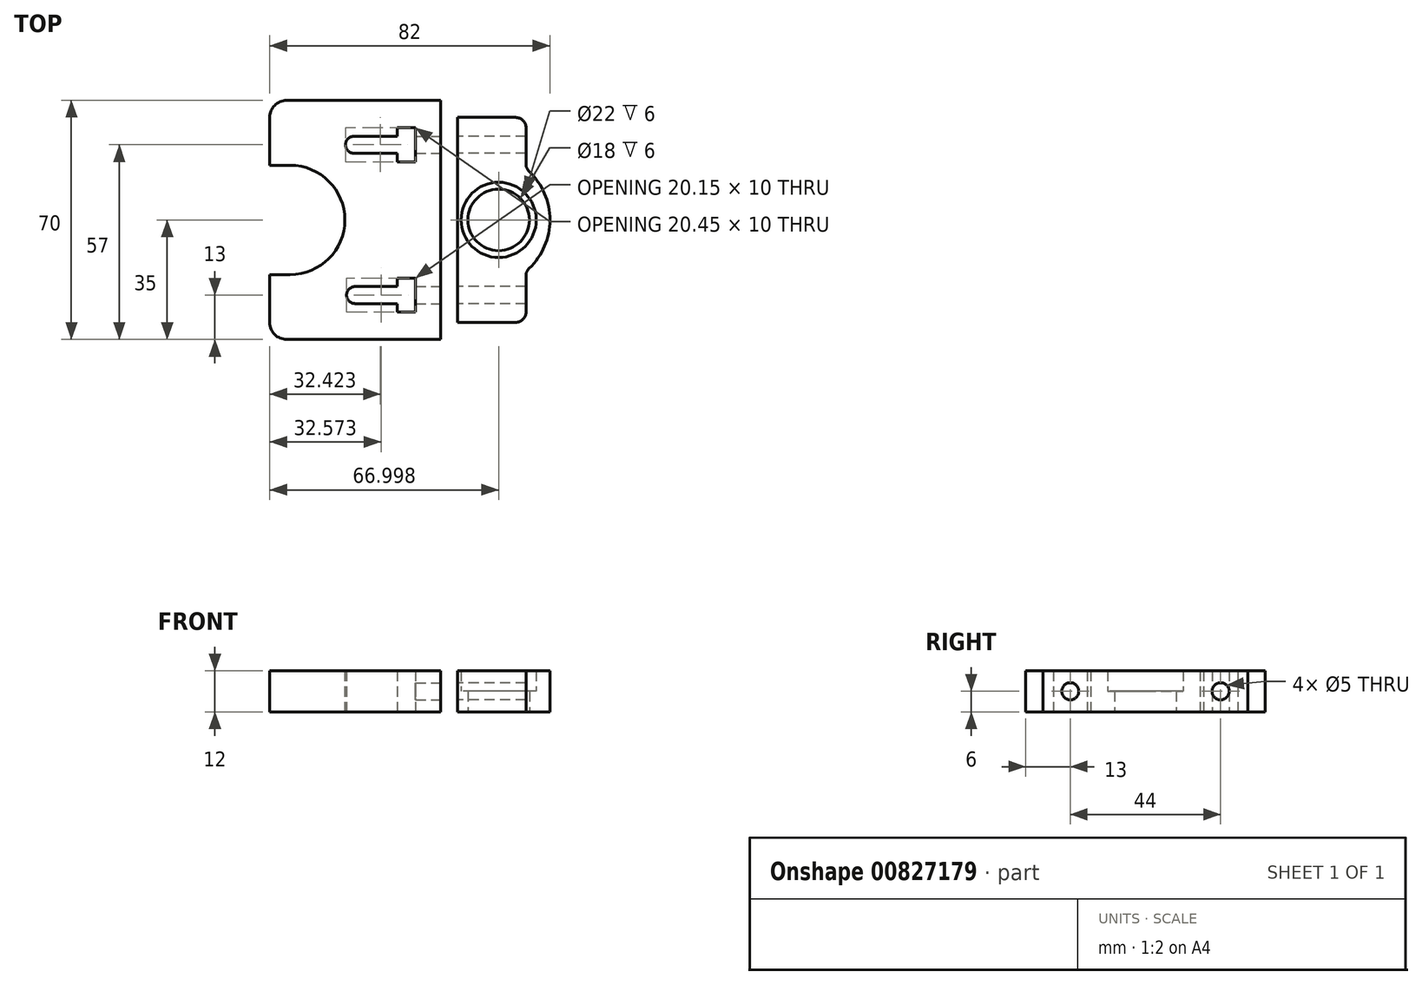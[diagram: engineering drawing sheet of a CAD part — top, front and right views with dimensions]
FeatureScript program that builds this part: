
annotation { "Feature Type Name" : "Feature", "Feature Type Description" : "" }
export const myFeature = defineFeature(function(context is Context, id is Id, definition is map)
    precondition{}
    {
        {
            var Q0;
            Q0=qCreatedBy(makeId("Top.planeOp"),FACE);
            var sketch = newSketch(context, id + "F0", { "sketchPlane" : qUnion([Q0])});
            skLineSegment(sketch, "E0.bottom", {"start": v(5.25, 143.35) * mm, "end": v(11.25, 143.35) * mm, "construction": true});
            skLineSegment(sketch, "E0.top", {"start": v(5.25, -56.65) * mm, "end": v(11.25, -56.65) * mm, "construction": true});
            skLineSegment(sketch, "E1", {"start": v(11.25, 0) * mm, "end": v(23.25, 0) * mm, "construction": true});
            skCircle(sketch, "E2", {"center": v(23.25, 0) * mm, "radius": 11 * mm, "construction": true});
            skLineSegment(sketch, "E3", {"start": v(23.25, 0) * mm, "end": v(-37.75, 0) * mm, "construction": true});
            skCircle(sketch, "E4", {"center": v(-37.75, 0) * mm, "radius": 12.5 * mm, "construction": true});
            skCircle(sketch, "E5", {"center": v(23.25, 0) * mm, "radius": 12.5 * mm, "construction": true});
            skCircle(sketch, "E6", {"center": v(-37.75, 0) * mm, "radius": 28 * mm, "construction": true});
            skLineSegment(sketch, "E7", {"start": v(6.25, 0) * mm, "end": v(6.25, 35) * mm});
            skLineSegment(sketch, "E8", {"start": v(6.25, 35) * mm, "end": v(-43.75, 35) * mm});
            skLineSegment(sketch, "E9", {"start": v(-43.75, 35) * mm, "end": v(-43.75, 16) * mm});
            skLineSegment(sketch, "E10", {"start": v(-43.75, -35) * mm, "end": v(6.25, -35) * mm});
            skLineSegment(sketch, "E11", {"start": v(6.25, -35) * mm, "end": v(6.25, 0) * mm});
            skLineSegment(sketch, "E12", {"start": v(-37.75, 16) * mm, "end": v(-43.75, 16) * mm});
            skLineSegment(sketch, "E13", {"start": v(-37.75, -16) * mm, "end": v(-43.75, -16) * mm});
            skArc(sketch, "E14.trimOffspring", {"start": v(-37.75, -16) * mm, "mid": v(-21.75, 0) * mm, "end": v(-37.75, 16) * mm});
            skLineSegment(sketch, "E15.trimOffspring", {"start": v(-43.75, -16) * mm, "end": v(-43.75, -35) * mm});
            skLineSegment(sketch, "E16", {"start": v(-37.75, -28) * mm, "end": v(6.25, -28) * mm, "construction": true});
            skLineSegment(sketch, "E17", {"start": v(-37.75, 28) * mm, "end": v(6.25, 28) * mm, "construction": true});
            skLineSegment(sketch, "E18", {"start": v(-37.75, 0) * mm, "end": v(-37.75, 16) * mm, "construction": true});
            skLineSegment(sketch, "E19", {"start": v(-37.75, 0) * mm, "end": v(-37.75, -16) * mm, "construction": true});
            skLineSegment(sketch, "E20", {"start": v(-37.75, 0) * mm, "end": v(-7.75, 0) * mm, "construction": true});
            skLineSegment(sketch, "E21", {"start": v(-7.75, 0) * mm, "end": v(-7.75, 22) * mm, "construction": true});
            skLineSegment(sketch, "E22", {"start": v(-7.75, 0) * mm, "end": v(-7.75, -22) * mm, "construction": true});
            skLineSegment(sketch, "E23", {"start": v(-7.75, 22) * mm, "end": v(-13.25, 22) * mm, "construction": true});
            skLineSegment(sketch, "E24", {"start": v(-7.75, -22) * mm, "end": v(-13.25, -22) * mm, "construction": true});
            skCircle(sketch, "E25", {"center": v(-13.25, -22) * mm, "radius": 2.5 * mm, "construction": true});
            skCircle(sketch, "E26", {"center": v(-13.25, 22) * mm, "radius": 2.5 * mm, "construction": true});
            skLineSegment(sketch, "E27", {"start": v(-13.25, -22) * mm, "end": v(-18.75, -22) * mm, "construction": true});
            skArc(sketch, "E28", {"start": v(-18.75, -19.5) * mm, "mid": v(-21.25, -22) * mm, "end": v(-18.75, -24.5) * mm});
            skLineSegment(sketch, "E29", {"start": v(-18.75, -22) * mm, "end": v(-18.75, -19.5) * mm, "construction": true});
            skLineSegment(sketch, "E30", {"start": v(-18.75, -19.5) * mm, "end": v(-18.75, -24.5) * mm, "construction": true});
            skLineSegment(sketch, "E31", {"start": v(-7.75, -22) * mm, "end": v(-7.75, -24.5) * mm, "construction": true});
            skLineSegment(sketch, "E32", {"start": v(-18.75, -19.5) * mm, "end": v(-6.4, -19.5) * mm});
            skLineSegment(sketch, "E33", {"start": v(-18.75, -24.5) * mm, "end": v(-6.4, -24.5) * mm});
            skArc(sketch, "E34", {"start": v(-19.05, 24.5) * mm, "mid": v(-21.55, 22) * mm, "end": v(-19.05, 19.5) * mm});
            skLineSegment(sketch, "E35", {"start": v(-13.25, 22) * mm, "end": v(31.35, 22) * mm, "construction": true});
            skLineSegment(sketch, "E36", {"start": v(-13.25, -22) * mm, "end": v(47, -22) * mm, "construction": true});
            skLineSegment(sketch, "E37", {"start": v(6.25, 22) * mm, "end": v(-3.75, 22) * mm, "construction": true});
            skLineSegment(sketch, "E38", {"start": v(6.25, -22) * mm, "end": v(-3.75, -22) * mm, "construction": true});
            skLineSegment(sketch, "E39.bottom", {"start": v(-1.1, 27) * mm, "end": v(-6.4, 27) * mm});
            skLineSegment(sketch, "E39.top", {"start": v(-1.1, 17) * mm, "end": v(-6.4, 17) * mm});
            skLineSegment(sketch, "E39.left", {"start": v(-1.1, 27) * mm, "end": v(-1.1, 17) * mm});
            skLineSegment(sketch, "E39.right", {"start": v(-6.4, 27) * mm, "end": v(-6.4, 17) * mm});
            skPoint(sketch, "E39.middle", {"position": v(-3.75, 22) * mm});
            skLineSegment(sketch, "E40.bottom", {"start": v(-1.1, -17) * mm, "end": v(-6.4, -17) * mm});
            skLineSegment(sketch, "E40.top", {"start": v(-1.1, -27) * mm, "end": v(-6.4, -27) * mm});
            skLineSegment(sketch, "E40.left", {"start": v(-1.1, -17) * mm, "end": v(-1.1, -27) * mm});
            skLineSegment(sketch, "E40.right", {"start": v(-6.4, -17) * mm, "end": v(-6.4, -27) * mm});
            skPoint(sketch, "E40.middle", {"position": v(-3.75, -22) * mm});
            skLineSegment(sketch, "E41", {"start": v(-19.05, 24.5) * mm, "end": v(-6.4, 24.5) * mm});
            skLineSegment(sketch, "E42", {"start": v(-19.05, 19.5) * mm, "end": v(-6.4, 19.5) * mm});
            skSolve(sketch);
        }
        {
            var Q0;
            Q0=makeQuery(id+"F0.imprint","IMPRINT",FACE,{"disambiguationData":[TD([[makeQuery(id+"F0.imprint","IMPRINT",EDGE,{"derivedFrom":sQuery(id+"F0.wireOp",EDGE,"E7")}),1.0]])]});
            extrude(context, id + "F1", {"entities" : qUnion([Q0]), "depth" : 12 * mm, "offsetDistance" : 25 * mm});
        }
        {
            var Q0;
            Q0=makeQuery(id+"F1.opExtrude","SWEPT_FACE",FACE,{"disambiguationData":[OSD([sQuery(id+"F0.wireOp",EDGE,"E7"),sQuery(id+"F0.wireOp",EDGE,"E11")])]});
            var sketch = newSketch(context, id + "F2", { "sketchPlane" : qUnion([Q0])});
            skLineSegment(sketch, "E43", {"start": v(-35, 12) * mm, "end": v(-22, 12) * mm, "construction": true});
            skLineSegment(sketch, "E44", {"start": v(-22, 12) * mm, "end": v(-22, 6) * mm, "construction": true});
            skLineSegment(sketch, "E45", {"start": v(35, 12) * mm, "end": v(22, 12) * mm, "construction": true});
            skLineSegment(sketch, "E46", {"start": v(22, 12) * mm, "end": v(22, 6) * mm, "construction": true});
            skLineSegment(sketch, "E47", {"start": v(-22, 12) * mm, "end": v(0, 12) * mm, "construction": true});
            skLineSegment(sketch, "E48", {"start": v(0, 12) * mm, "end": v(22, 12) * mm, "construction": true});
            skCircle(sketch, "E49", {"center": v(-22, 6) * mm, "radius": 2.5 * mm});
            skCircle(sketch, "E50", {"center": v(22, 6) * mm, "radius": 2.5 * mm});
            skSolve(sketch);
        }
        {
            var Q0;
            Q0 = qSketchRegion(id + "F2", true);
            extrude(context, id + "F3", {"entities" : qUnion([Q0]), "operationType" : NewBodyOperationType.REMOVE, "oppositeDirection" : true, "depth" : 15 * mm, "offsetDistance" : 25 * mm});
        }
        {
            var Q0;
            Q0=makeQuery(id+"F1.opExtrude","SWEPT_EDGE",EDGE,{"disambiguationData":[OSD([sQuery(id+"F0.wireOp",EDGE,"E8"),sQuery(id+"F0.wireOp",EDGE,"E9")])]});
            var Q1;
            Q1=makeQuery(id+"F1.opExtrude","SWEPT_EDGE",EDGE,{"disambiguationData":[OSD([sQuery(id+"F0.wireOp",EDGE,"E10"),sQuery(id+"F0.wireOp",EDGE,"E15.trimOffspring")])]});
            fillet(context, id + "F4", {"entities" : qUnion([Q0, Q1]), "radius" : 5 * mm, "tangentPropagation" : true, "allowEdgeOverflow" : false});
        }
        {
            var Q0;
            Q0=qCreatedBy(makeId("Top.planeOp"),FACE);
            var sketch = newSketch(context, id + "F5", { "sketchPlane" : qUnion([Q0])});
            skLineSegment(sketch, "E51.bottom", {"start": v(11.25, 30) * mm, "end": v(31.25, 30) * mm});
            skLineSegment(sketch, "E51.top", {"start": v(11.25, -30) * mm, "end": v(31.25, -30) * mm});
            skLineSegment(sketch, "E52", {"start": v(31.25, 30) * mm, "end": v(31.25, 15) * mm});
            skLineSegment(sketch, "E53", {"start": v(31.25, -30) * mm, "end": v(31.25, -15) * mm});
            skLineSegment(sketch, "E54", {"start": v(6.25, 0) * mm, "end": v(23.25, 0) * mm, "construction": true});
            skCircle(sketch, "E55", {"center": v(23.25, 0) * mm, "radius": 11 * mm});
            skLineSegment(sketch, "E56", {"start": v(11.25, -30) * mm, "end": v(11.25, 30) * mm});
            skCircle(sketch, "E57", {"center": v(23.25, 0) * mm, "radius": 9 * mm});
            skLineSegment(sketch, "E58", {"start": v(6.25, 0) * mm, "end": v(11.25, 0) * mm, "construction": true});
            skPoint(sketch, "E59", {"position": v(6.25, 0) * mm});
            skLineSegment(sketch, "E60", {"start": v(23.25, 0) * mm, "end": v(38.25, 0) * mm, "construction": true});
            skArc(sketch, "E61", {"start": v(31.25, -15) * mm, "mid": v(38.25, 0) * mm, "end": v(31.25, 15) * mm});
            skSolve(sketch);
        }
        {
            var Q0;
            Q0=makeQuery(id+"F5.imprint","IMPRINT",FACE,{"disambiguationData":[TD([[makeQuery(id+"F5.imprint","IMPRINT",EDGE,{"derivedFrom":sQuery(id+"F5.wireOp",EDGE,"E51.bottom")}),-1.0]])]});
            extrude(context, id + "F6", {"entities" : qUnion([Q0]), "operationType" : NewBodyOperationType.ADD, "depth" : 12 * mm, "offsetDistance" : 25 * mm});
        }
        {
            var Q0;
            Q0=makeQuery(id+"F5.imprint","IMPRINT",FACE,{"disambiguationData":[TD([[makeQuery(id+"F5.imprint","IMPRINT",EDGE,{"derivedFrom":sQuery(id+"F5.wireOp",EDGE,"E55")}),1.0]])]});
            extrude(context, id + "F7", {"entities" : qUnion([Q0]), "operationType" : NewBodyOperationType.ADD, "depth" : 6 * mm, "offsetDistance" : 25 * mm});
        }
        {
            var Q0;
            Q0=makeQuery(id+"F6.opExtrude","SWEPT_EDGE",EDGE,{"disambiguationData":[OSD([sQuery(id+"F5.wireOp",EDGE,"E51.right"),sQuery(id+"F5.wireOp",EDGE,"c0CEKEwx-10Q6-sSKC-CvlY-BkYtkLKJvecI")])]});
            var Q1;
            Q1=makeQuery(id+"F6.opExtrude","SWEPT_EDGE",EDGE,{"disambiguationData":[OSD([sQuery(id+"F5.wireOp",EDGE,"E52"),sQuery(id+"F5.wireOp",EDGE,"c0CEKEwx-10Q6-sSKC-CvlY-BkYtkLKJvecI")])]});
            var Q2;
            Q2=makeQuery(id+"F6.opExtrude","SWEPT_EDGE",EDGE,{"disambiguationData":[OSD([sQuery(id+"F5.wireOp",EDGE,"E51.right"),sQuery(id+"F5.wireOp",EDGE,"G2N44dxP-Yb7r-ZY3g-j65f-KiLg5HQXxyeu")])]});
            var Q3;
            Q3=makeQuery(id+"F6.opExtrude","SWEPT_EDGE",EDGE,{"disambiguationData":[OSD([sQuery(id+"F5.wireOp",EDGE,"E53"),sQuery(id+"F5.wireOp",EDGE,"G2N44dxP-Yb7r-ZY3g-j65f-KiLg5HQXxyeu")])]});
            var Q4;
            Q4=makeQuery(id+"F6.opExtrude","SWEPT_EDGE",EDGE,{"disambiguationData":[OSD([sQuery(id+"F5.wireOp",EDGE,"E51.bottom"),sQuery(id+"F5.wireOp",EDGE,"E52")])]});
            var Q5;
            Q5=makeQuery(id+"F6.opExtrude","SWEPT_EDGE",EDGE,{"disambiguationData":[OSD([sQuery(id+"F5.wireOp",EDGE,"E51.top"),sQuery(id+"F5.wireOp",EDGE,"E53")])]});
            fillet(context, id + "F8", {"entities" : qUnion([Q0, Q1, Q2, Q3, Q4, Q5]), "radius" : 3 * mm, "tangentPropagation" : true, "allowEdgeOverflow" : false});
        }
        {
            var Q0;
            Q0 = qSketchRegion(id + "F2", true);
            var Q1;
            Q1=makeQuery(id+"F6.opExtrude","SWEPT_FACE",FACE,{"disambiguationData":[OSD([sQuery(id+"F5.wireOp",EDGE,"E52")])]});
            extrude(context, id + "F9", {"entities" : qUnion([Q0, Q1]), "operationType" : NewBodyOperationType.REMOVE, "depth" : 25 * mm, "offsetDistance" : 25 * mm});
        }
    });
